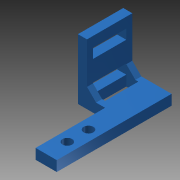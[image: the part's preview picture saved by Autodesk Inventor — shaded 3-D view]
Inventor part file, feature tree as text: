
AUTODESK INVENTOR PART (.ipt)
format: ipt  version: 2013 SP2 (Build 170200200, 200)  size: 127,488 bytes
history: native  units: mm
features: extrude x3, sketch x3, chamfer x1
ambient origin geometry x8: Origin, YZ Plane, XZ Plane, XY Plane, X Axis, Y Axis, Z Axis, Center Point
bodies: Solid1 (feature_tree)
feature tree (7):
  extrude  "Extrusion1"  Depth=38.0mm
  extrude  "Extrusion2"  Depth=3.2mm
  chamfer  "Chamfer1"  Distance=7.0mm
  extrude  "Extrusion3"  Depth=15.0mm
  sketch  "Sketch1"  dims[d0=7.0mm d1=38.0mm]
  sketch  "Sketch2"  dims[d2=3.2mm d3=3.2mm]
  sketch  "Sketch3"  dims[d4=7.0mm d5=7.0mm d7=15.0mm d8=16.0mm d9=3.4mm d10=0.0mm d11=20.0mm d12=2.0mm d13=2.0mm d14=3.2mm d15=3.4mm d16=6.8mm d17=3.2mm d18=3.0mm d19=0.0mm d20=4.0mm d21=3.0mm d22=2.0mm d23=45.0deg d24=4.0mm d25=0.0mm]
